# Revit family: Elite_Sliding_Window_XXXX_Custom
name_source: partatom
category: Windows
revit_build: Autodesk Revit 2014 (Build: 20130308_1515(x64)
units: mm (PartAtom-declared; Revit-internal decimal feet)

## types (1)
- EliteSW-XXXX-Custom
    Area Middle Sash Glazing = 0.23 m²
    Area Side Sash Glazing = 0.23 m²
    Astragal Sash Gap = 1 mm  [stored 0.00328084 ft]
    Centered In Wall = Yes
    Custom Frame Offset From Exterior = 0 mm  [stored 0 ft]
    Custom Sash Width Side = 800 mm  [stored 2.62467 ft]
    Custom Windload = 1000 mm  [stored 3.28084 ft]
    Custom Window Height = 590 mm  [stored 1.9357 ft]
    Custom Window Width = 2390 mm  [stored 7.84121 ft]
    Default Sill Height = 800 mm  [stored 2.62467 ft]
    Description = Sliding window, XXXX custom
    Equal Sash Width = Yes
    Frame Thickness = 70 mm
    Height = 590 mm  [stored 1.9357 ft]
    Inside Heavy Duty Interlocker = No
    Interlocker Configuration = 0 mm  [stored 0 ft]
    Limit Sash Height Max = 1800 mm  [stored 5.90551 ft]
    Limit Sash Height Min = 300 mm  [stored 0.984252 ft]
    Limit Sash Width Max = 1500 mm  [stored 4.92126 ft]
    Limit Sash Width Min = 300 mm  [stored 0.984252 ft]
    Limit Sash Width Side Max = 912 mm
    Limit Sash Width Side Min = 300 mm  [stored 0.984252 ft]
    Limit Window Height Max = 1883 mm
    Limit Window Height Min = 383 mm  [stored 1.25656 ft]
    Limit Window Width Max = 2990 mm
    Limit Window Width Min = 1167 mm
    Manufacturer = Crealco
    Max Pane Area = 0.23 m²
    Model = Elite
    Outside Heavy Duty Interlocker = No
    Sash Frame Seal = 1 mm  [stored 0.00328084 ft]
    Sash Height = 507 mm  [stored 1.66339 ft]
    Sash Rail Fore Aft Spacing = 5 mm  [stored 0.0164042 ft]
    Sash Side Spacing = 1 mm  [stored 0.00328084 ft]
    Sash Width Middle = 606 mm
    Sash Width Sides = 606 mm
    URL = http://www.crealco.co.za
    Wall Closure = By host
    Width = 2390 mm  [stored 7.84121 ft]
    Windload Design = 1000 mm  [stored 3.28084 ft]

note: [stored X ft] marks values corroborated as IEEE doubles in the binary element streams (Revit-internal decimal feet)

## geometry (parser evidence)
native form markers: Sweep x33
no freeform markers — native parametric forms only
